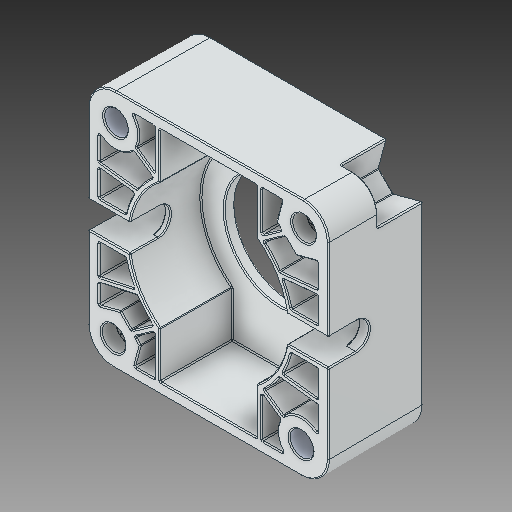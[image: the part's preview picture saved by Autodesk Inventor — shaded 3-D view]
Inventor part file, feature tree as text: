
AUTODESK INVENTOR PART (.ipt)
format: ipt  version: 2019 (Build 230136000, 136)  size: 1,304,064 bytes
history: native  units: in
note: dims shown in document units (in); Inventor stores cm internally (conversion verified against a paired STEP export)
features: fillet x1
ambient origin geometry x8: Origin, YZ Plane, XZ Plane, XY Plane, X Axis, Y Axis, Z Axis, Center Point
bodies: Solid1 (feature_tree)
feature tree (1):
  fillet  "Fillet7"  [1 undecoded]
note: 1 required parameter value undecoded (feature->parameter linkage not recoverable at this tier; creation-order binding heuristic only, values carry confidence <= 0.55)
